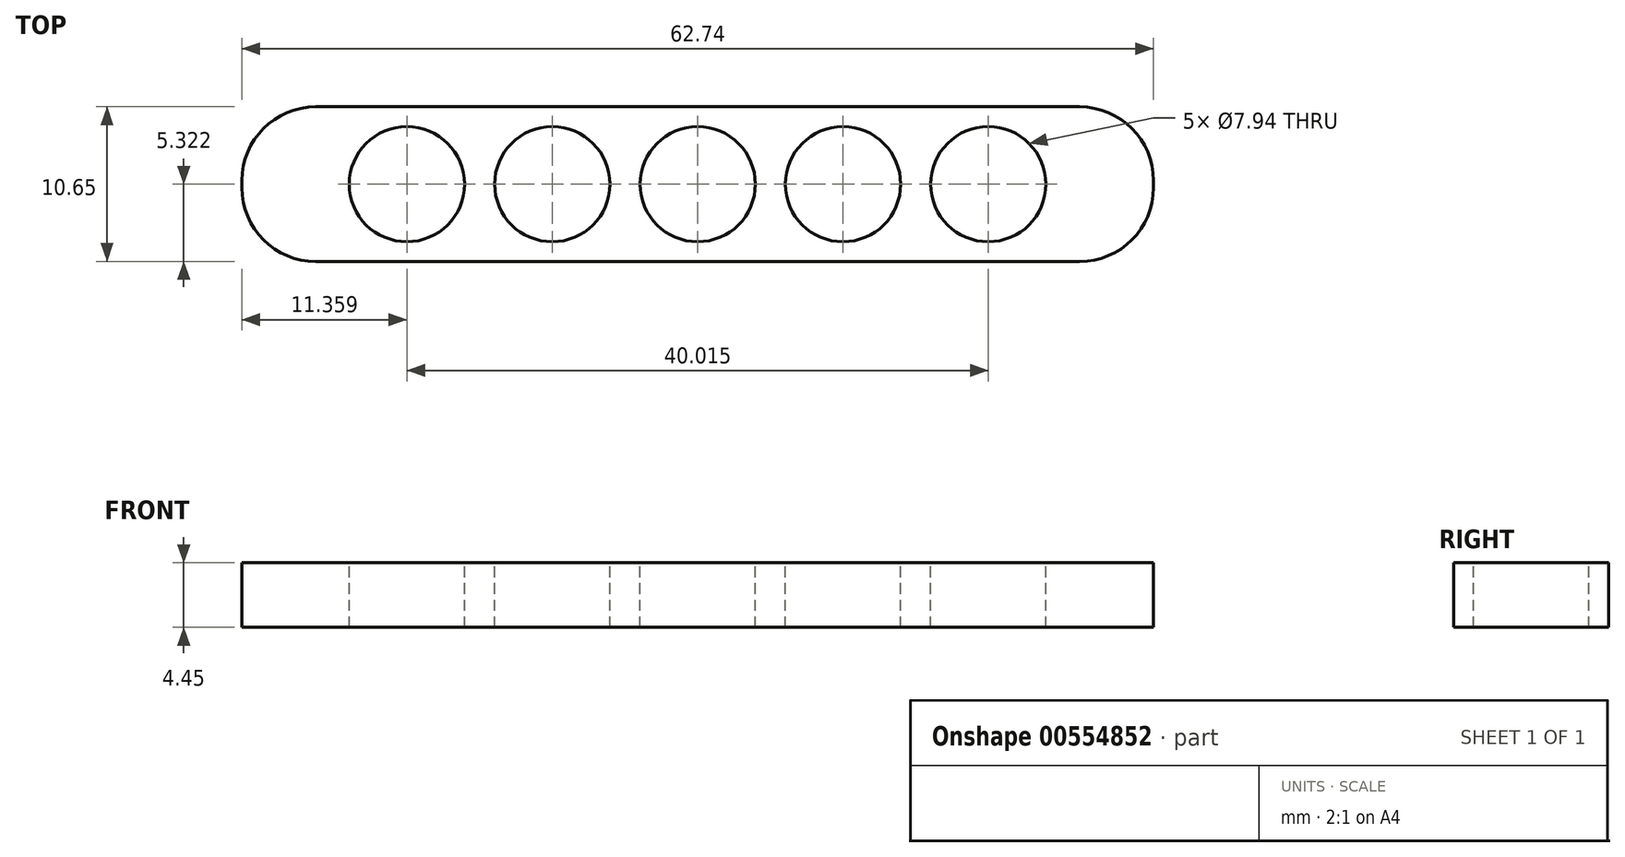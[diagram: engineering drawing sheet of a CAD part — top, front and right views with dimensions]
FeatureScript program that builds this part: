
annotation { "Feature Type Name" : "Feature", "Feature Type Description" : "" }
export const myFeature = defineFeature(function(context is Context, id is Id, definition is map)
    precondition{}
    {
        {
            var Q0;
            Q0=qCreatedBy(makeId("Top.planeOp"),FACE);
            var sketch = newSketch(context, id + "F0", { "sketchPlane" : qUnion([Q0])});
            skLineSegment(sketch, "E0.bottom", {"start": v(-46.34, 3.17) * mm, "end": v(16.4, 3.17) * mm});
            skLineSegment(sketch, "E0.top", {"start": v(-46.34, -7.48) * mm, "end": v(16.4, -7.48) * mm});
            skLineSegment(sketch, "E0.left", {"start": v(-46.34, 3.17) * mm, "end": v(-46.34, -7.48) * mm});
            skLineSegment(sketch, "E0.right", {"start": v(16.4, 3.17) * mm, "end": v(16.4, -7.48) * mm});
            skSolve(sketch);
        }
        {
            var Q0;
            Q0=makeQuery(id+"F0.imprint","IMPRINT",FACE,{"disambiguationData":[TD([[makeQuery(id+"F0.imprint","IMPRINT",EDGE,{"derivedFrom":sQuery(id+"F0.wireOp",EDGE,"E0.bottom")}),-1.0]])]});
            extrude(context, id + "F1", {"entities" : qUnion([Q0]), "depth" : 4.44 * mm, "offsetDistance" : 25.4 * mm});
        }
        {
            var Q0;
            Q0=makeQuery(id+"F1.opExtrude","CAP_FACE",FACE,{"disambiguationData":[OSD([sQuery(id+"F0.wireOp",EDGE,"E0.bottom"),sQuery(id+"F0.wireOp",EDGE,"E0.top"),sQuery(id+"F0.wireOp",EDGE,"E0.left"),sQuery(id+"F0.wireOp",EDGE,"E0.right")])],"isStart":false});
            var sketch = newSketch(context, id + "F2", { "sketchPlane" : qUnion([Q0])});
            skCircle(sketch, "E1", {"center": v(-14.97, -2.16) * mm, "radius": 3.97 * mm});
            skPoint(sketch, "E2.center.orphan", {"position": v(-31.7, -2.16) * mm});
            skPoint(sketch, "E3.center.orphan", {"position": v(-42, -2.16) * mm});
            skPoint(sketch, "E4.orphan", {"position": v(-14.97, 3.17) * mm});
            skPoint(sketch, "E5.end.orphan", {"position": v(-14.97, -7.48) * mm});
            skCircle(sketch, "E6.1.0.0", {"center": v(-4.97, -2.16) * mm, "radius": 3.97 * mm});
            skCircle(sketch, "E6.2.0.0", {"center": v(5.03, -2.16) * mm, "radius": 3.97 * mm});
            skLineSegment(sketch, "E6.direction1", {"start": v(-14.97, -2.16) * mm, "end": v(-4.97, -2.16) * mm, "construction": true});
            skCircle(sketch, "E7.1.0.0", {"center": v(-24.97, -2.16) * mm, "radius": 3.97 * mm});
            skCircle(sketch, "E7.2.0.0", {"center": v(-34.98, -2.16) * mm, "radius": 3.97 * mm});
            skLineSegment(sketch, "E7.direction1", {"start": v(-14.97, -2.16) * mm, "end": v(-24.97, -2.16) * mm, "construction": true});
            skSolve(sketch);
        }
        {
            var Q0;
            Q0=makeQuery(id+"F2.imprint","IMPRINT",FACE,{"disambiguationData":[TD([[makeQuery(id+"F2.imprint","IMPRINT",EDGE,{"derivedFrom":sQuery(id+"F2.wireOp",EDGE,"E7.2.0.0")}),1.0]])]});
            var Q1;
            Q1=makeQuery(id+"F2.imprint","IMPRINT",FACE,{"disambiguationData":[TD([[makeQuery(id+"F2.imprint","IMPRINT",EDGE,{"derivedFrom":sQuery(id+"F2.wireOp",EDGE,"E6.2.0.0")}),1.0]])]});
            var Q2;
            Q2=makeQuery(id+"F2.imprint","IMPRINT",FACE,{"disambiguationData":[TD([[makeQuery(id+"F2.imprint","IMPRINT",EDGE,{"derivedFrom":sQuery(id+"F2.wireOp",EDGE,"E7.1.0.0")}),1.0]])]});
            var Q3;
            Q3=makeQuery(id+"F2.imprint","IMPRINT",FACE,{"disambiguationData":[TD([[makeQuery(id+"F2.imprint","IMPRINT",EDGE,{"derivedFrom":sQuery(id+"F2.wireOp",EDGE,"E1")}),1.0]])]});
            var Q4;
            Q4=makeQuery(id+"F2.imprint","IMPRINT",FACE,{"disambiguationData":[TD([[makeQuery(id+"F2.imprint","IMPRINT",EDGE,{"derivedFrom":sQuery(id+"F2.wireOp",EDGE,"E6.1.0.0")}),1.0]])]});
            extrude(context, id + "F3", {"entities" : qUnion([Q0, Q1, Q2, Q3, Q4]), "operationType" : NewBodyOperationType.REMOVE, "endBound" : BoundingType.THROUGH_ALL, "oppositeDirection" : true, "depth" : 3.17 * mm, "offsetDistance" : 25.4 * mm});
        }
        {
            var Q0;
            Q0=makeQuery(id+"F1.opExtrude","SWEPT_EDGE",EDGE,{"disambiguationData":[OSD([sQuery(id+"F0.wireOp",EDGE,"E0.bottom"),sQuery(id+"F0.wireOp",EDGE,"E0.left")])]});
            var Q1;
            Q1=makeQuery(id+"F1.opExtrude","SWEPT_EDGE",EDGE,{"disambiguationData":[OSD([sQuery(id+"F0.wireOp",EDGE,"E0.top"),sQuery(id+"F0.wireOp",EDGE,"E0.left")])]});
            fillet(context, id + "F4", {"entities" : qUnion([Q0, Q1]), "radius" : 5.08 * mm, "tangentPropagation" : true, "allowEdgeOverflow" : false});
        }
        {
            var Q0;
            Q0=makeQuery(id+"F1.opExtrude","SWEPT_EDGE",EDGE,{"disambiguationData":[OSD([sQuery(id+"F0.wireOp",EDGE,"E0.top"),sQuery(id+"F0.wireOp",EDGE,"E0.right")])]});
            var Q1;
            Q1=makeQuery(id+"F1.opExtrude","SWEPT_EDGE",EDGE,{"disambiguationData":[OSD([sQuery(id+"F0.wireOp",EDGE,"E0.bottom"),sQuery(id+"F0.wireOp",EDGE,"E0.right")])]});
            fillet(context, id + "F5", {"entities" : qUnion([Q0, Q1]), "radius" : 5.08 * mm, "tangentPropagation" : true, "allowEdgeOverflow" : false});
        }
    });
